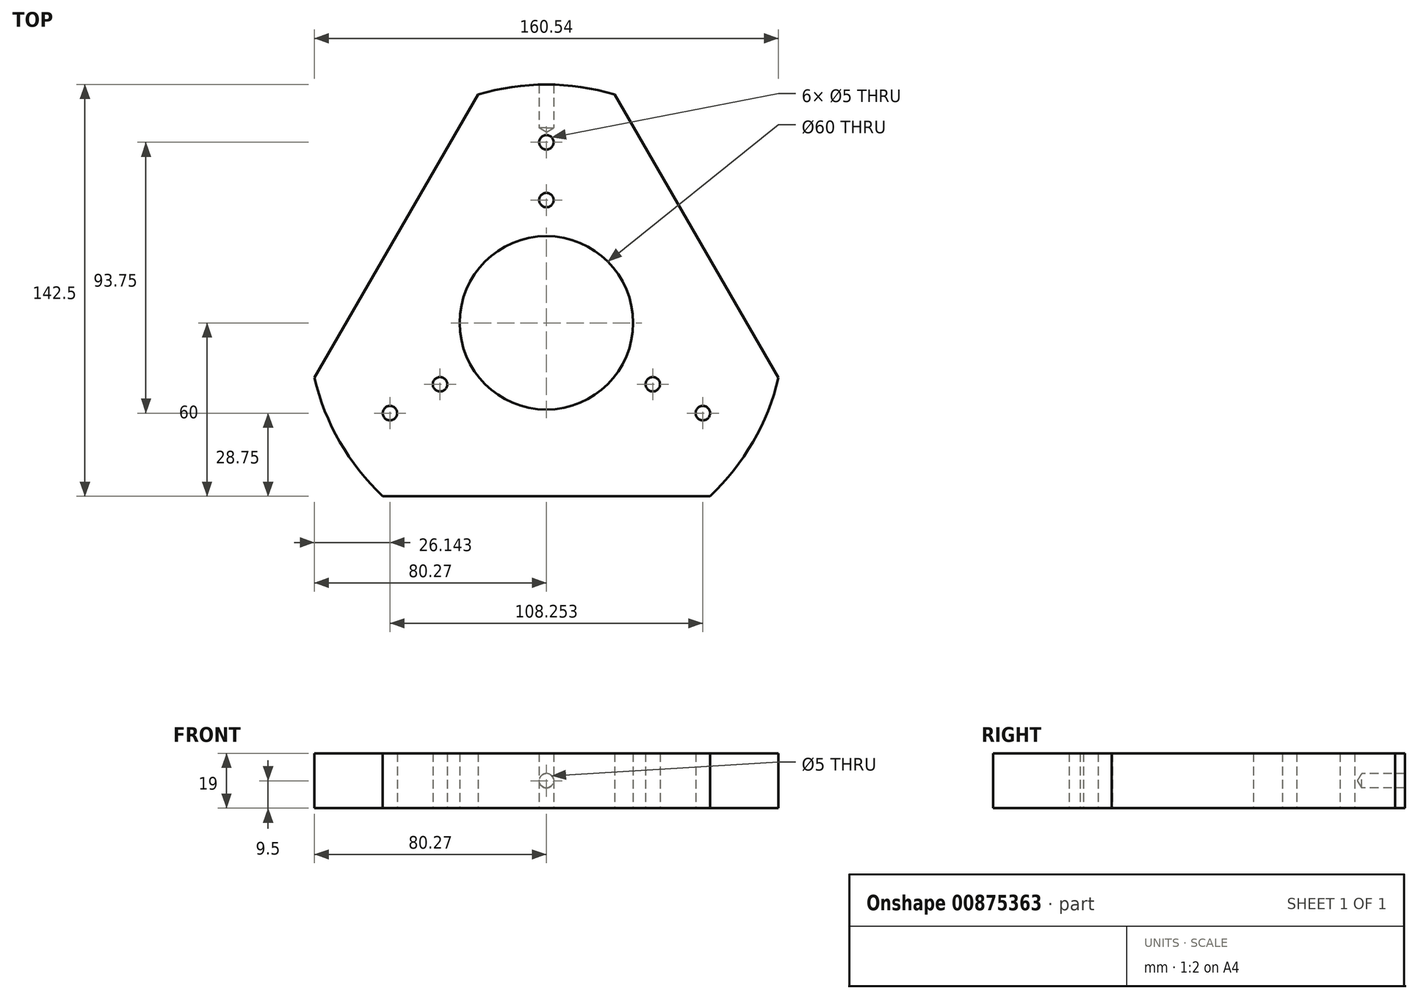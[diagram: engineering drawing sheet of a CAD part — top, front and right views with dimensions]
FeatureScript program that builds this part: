
annotation { "Feature Type Name" : "Feature", "Feature Type Description" : "" }
export const myFeature = defineFeature(function(context is Context, id is Id, definition is map)
    precondition{}
    {
        {
            var Q0;
            Q0=qCreatedBy(makeId("Top.planeOp"),FACE);
            var sketch = newSketch(context, id + "F0", { "sketchPlane" : qUnion([Q0])});
            skCircle(sketch, "E0", {"center": v(0, 0) * mm, "radius": 60 * mm, "construction": true});
            skCircle(sketch, "E1", {"center": v(0, 0) * mm, "radius": 30 * mm});
            skCircle(sketch, "E2.0", {"center": v(0, 0) * mm, "radius": 62.5 * mm, "construction": true});
            skCircle(sketch, "E3", {"center": v(0, 62.5) * mm, "radius": 2.5 * mm});
            skCircle(sketch, "E4.1.0", {"center": v(-54.13, -31.25) * mm, "radius": 2.5 * mm});
            skCircle(sketch, "E4.2.0", {"center": v(54.13, -31.25) * mm, "radius": 2.5 * mm});
            skCircle(sketch, "E5", {"center": v(0, 0) * mm, "radius": 42.5 * mm, "construction": true});
            skCircle(sketch, "E6", {"center": v(0, 42.5) * mm, "radius": 2.5 * mm});
            skCircle(sketch, "E7.1.0", {"center": v(-36.8, -21.25) * mm, "radius": 2.5 * mm});
            skCircle(sketch, "E7.2.0", {"center": v(36.8, -21.25) * mm, "radius": 2.5 * mm});
            skCircle(sketch, "E8", {"center": v(0, 0) * mm, "radius": 82.5 * mm, "construction": true});
            skLineSegment(sketch, "E9", {"start": v(-117.16, 0) * mm, "end": v(115.25, 0) * mm, "construction": true});
            skLineSegment(sketch, "E10", {"start": v(0, 104.6) * mm, "end": v(0, -108.33) * mm, "construction": true});
            skLineSegment(sketch, "E11", {"start": v(0, 82.5) * mm, "end": v(0, 60) * mm, "construction": true});
            skLineSegment(sketch, "E12", {"start": v(0, 120) * mm, "end": v(103.92, -60) * mm, "construction": true});
            skLineSegment(sketch, "E13", {"start": v(103.92, -60) * mm, "end": v(-103.92, -60) * mm, "construction": true});
            skLineSegment(sketch, "E14", {"start": v(-103.92, -60) * mm, "end": v(0, 120) * mm, "construction": true});
            skLineSegment(sketch, "E15", {"start": v(23.65, 79.04) * mm, "end": v(80.27, -19.04) * mm});
            skLineSegment(sketch, "E16", {"start": v(-23.65, 79.04) * mm, "end": v(-80.27, -19.04) * mm});
            skLineSegment(sketch, "E17", {"start": v(-56.62, -60) * mm, "end": v(56.62, -60) * mm});
            skArc(sketch, "E18", {"start": v(56.62, -60) * mm, "mid": v(71.45, -41.25) * mm, "end": v(80.27, -19.04) * mm});
            skArc(sketch, "E19", {"start": v(23.65, 79.04) * mm, "mid": v(0, 82.5) * mm, "end": v(-23.65, 79.04) * mm});
            skArc(sketch, "E20", {"start": v(-80.27, -19.04) * mm, "mid": v(-71.45, -41.25) * mm, "end": v(-56.62, -60) * mm});
            skSolve(sketch);
        }
        {
            var Q0;
            Q0 = qSketchRegion(id + "F0", true);
            extrude(context, id + "F1", {"entities" : qUnion([Q0]), "depth" : 19 * mm, "offsetDistance" : 25 * mm});
        }
        {
            var Q0;
            Q0=qCreatedBy(makeId("Front.planeOp"),FACE);
            cPlane(context, id + "F2", {"entities" : qUnion([Q0]), "cplaneType" : CPlaneType.OFFSET, "offset" : (165 / 2) * mm, "oppositeDirection" : true, "width" : 150 * mm, "height" : 150 * mm});
        }
        {
            var Q0;
            Q0=qCreatedBy(id+"F2.planeOp",FACE);
            var sketch = newSketch(context, id + "F3", { "sketchPlane" : qUnion([Q0])});
            skLineSegment(sketch, "E21", {"start": v(0, 0) * mm, "end": v(0, 19) * mm, "construction": true});
            skPoint(sketch, "E22", {"position": v(0, 9.5) * mm});
            skSolve(sketch);
        }
        {
            var Q0;
            Q0=qCreatedBy(makeId("Front.planeOp"),FACE);
            var sketch = newSketch(context, id + "F4", { "sketchPlane" : qUnion([Q0])});
            skLineSegment(sketch, "E23", {"start": v(0, 0) * mm, "end": v(0, 41.15) * mm, "construction": true});
            skSolve(sketch);
        }
        {
            var Q0;
            Q0=sQuery(id+"F3.wireOp",VERTEX,"E22");
            var Q1;
            Q1=sQuery(id+"FVk42rkRE2kavS2_1.1.F3.wireOp",VERTEX,"E22");
            var Q2;
            Q2=sQuery(id+"FVk42rkRE2kavS2_1.2.F3.wireOp",VERTEX,"E22");
            var Q3;
            Q3=makeQuery(id+"F1.opExtrude","SWEPT_BODY",BODY,{"disambiguationData":[OSD([sQuery(id+"F0.wireOp",EDGE,"E1"),sQuery(id+"F0.wireOp",EDGE,"E3"),sQuery(id+"F0.wireOp",EDGE,"E4.1.0"),sQuery(id+"F0.wireOp",EDGE,"E4.2.0"),sQuery(id+"F0.wireOp",EDGE,"E6"),sQuery(id+"F0.wireOp",EDGE,"E7.1.0"),sQuery(id+"F0.wireOp",EDGE,"E7.2.0"),sQuery(id+"F0.wireOp",EDGE,"E15"),sQuery(id+"F0.wireOp",EDGE,"E16"),sQuery(id+"F0.wireOp",EDGE,"E17"),sQuery(id+"F0.wireOp",EDGE,"E18"),sQuery(id+"F0.wireOp",EDGE,"E19"),sQuery(id+"F0.wireOp",EDGE,"E20")])]});
            hole(context, id + "F5", {"style" : HoleStyle.SIMPLE, "endStyle" : HoleEndStyle.BLIND, "oppositeDirection" : true, "standardTappedOrClearance" : lookupTablePath({ "standard" : "ISO", "engagement" : "75%", "pitch" : "1 mm", "size" : "M6", "type" : "Tapped" }), "standardBlindInLast" : lookupTablePath({ "standard" : "ISO", "engagement" : "75%", "pitch" : "1 mm", "size" : "M6", "type" : "Tapped" }), "holeDiameter" : 5 * mm, "majorDiameter" : 6 * mm, "showTappedDepth" : true, "holeDepth" : 15 * mm, "isTappedThrough" : true, "tappedDepth" : 12 * mm, "tapClearance" : 3, "locations" : qUnion([Q0, Q1, Q2]), "scope" : qUnion([Q3]), "startStyle" : HoleStartStyle.SKETCH});
        }
    });
